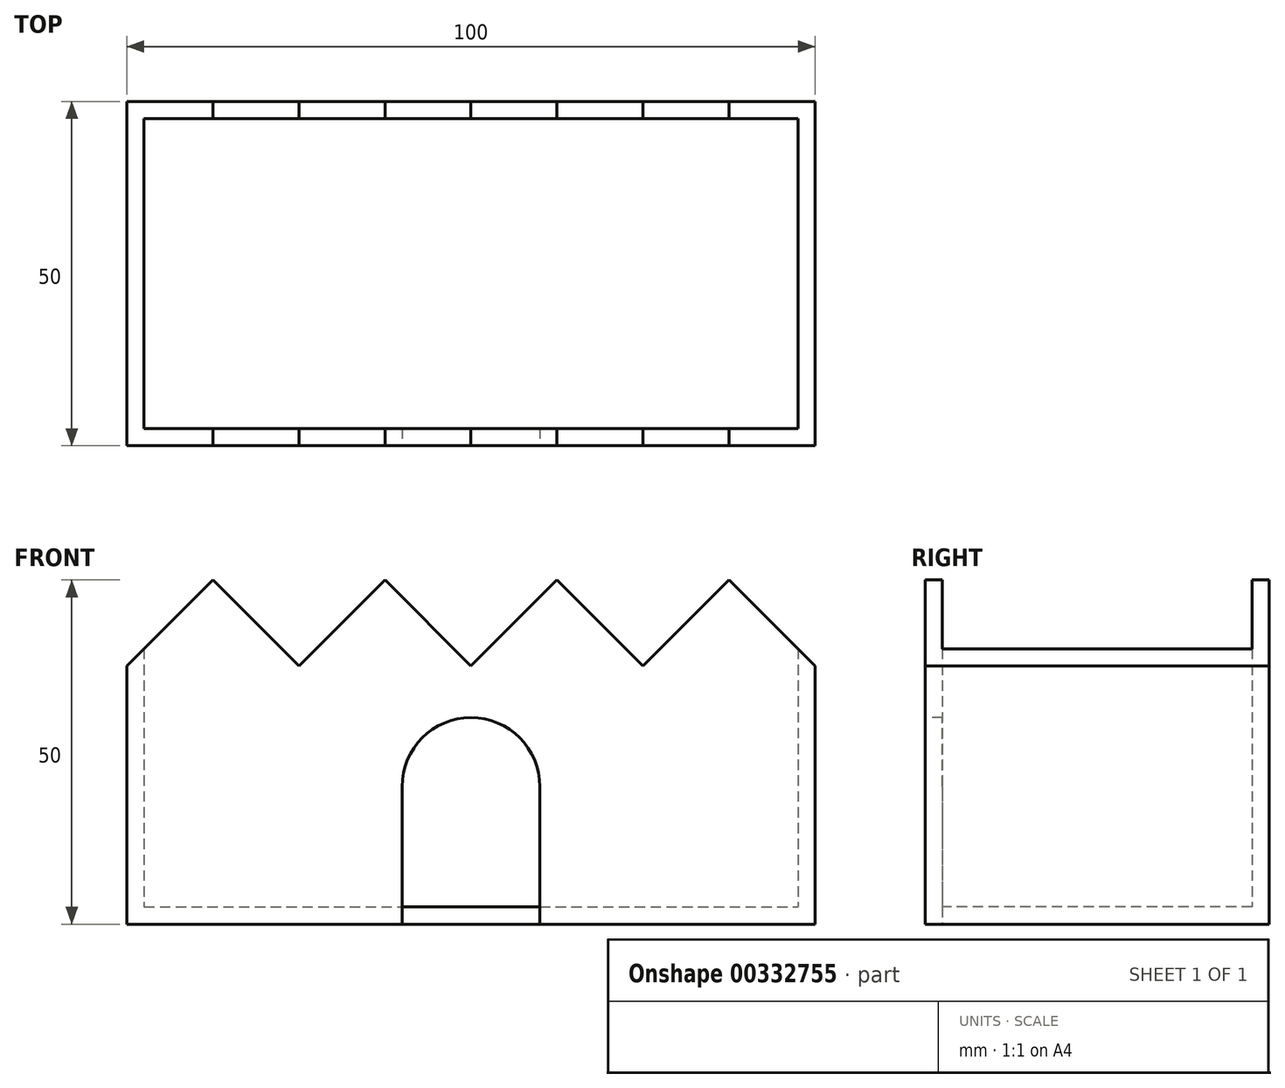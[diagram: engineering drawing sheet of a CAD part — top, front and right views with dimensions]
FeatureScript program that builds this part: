
annotation { "Feature Type Name" : "Feature", "Feature Type Description" : "" }
export const myFeature = defineFeature(function(context is Context, id is Id, definition is map)
    precondition{}
    {
        {
            var Q0;
            Q0=qCreatedBy(makeId("Top.planeOp"),FACE);
            var sketch = newSketch(context, id + "F0", { "sketchPlane" : qUnion([Q0])});
            skLineSegment(sketch, "E0.bottom", {"start": v(-50, 25) * mm, "end": v(50, 25) * mm});
            skLineSegment(sketch, "E0.top", {"start": v(-50, -25) * mm, "end": v(50, -25) * mm});
            skLineSegment(sketch, "E0.left", {"start": v(-50, 25) * mm, "end": v(-50, -25) * mm});
            skLineSegment(sketch, "E0.right", {"start": v(50, 25) * mm, "end": v(50, -25) * mm});
            skPoint(sketch, "E0.middle", {"position": v(0, 0) * mm});
            skSolve(sketch);
        }
        {
            var Q0;
            Q0=makeQuery(id+"F0.imprint","IMPRINT",FACE,{"disambiguationData":[TD([[makeQuery(id+"F0.imprint","IMPRINT",EDGE,{"derivedFrom":sQuery(id+"F0.wireOp",EDGE,"E0.bottom")}),-1.0]])]});
            extrude(context, id + "F1", {"entities" : qUnion([Q0]), "depth" : 50 * mm});
        }
        {
            var Q0;
            Q0=makeQuery(id+"F1.opExtrude","SWEPT_FACE",FACE,{"disambiguationData":[OSD([sQuery(id+"F0.wireOp",EDGE,"E0.top")])]});
            var sketch = newSketch(context, id + "F2", { "sketchPlane" : qUnion([Q0])});
            skLineSegment(sketch, "E1", {"start": v(-50, 37.5) * mm, "end": v(-37.5, 50) * mm});
            skLineSegment(sketch, "E2", {"start": v(-37.5, 50) * mm, "end": v(-25, 37.5) * mm});
            skLineSegment(sketch, "E3", {"start": v(-25, 37.5) * mm, "end": v(-12.5, 50) * mm});
            skLineSegment(sketch, "E4", {"start": v(-12.5, 50) * mm, "end": v(0, 37.5) * mm});
            skLineSegment(sketch, "E5", {"start": v(0, 37.5) * mm, "end": v(12.5, 50) * mm});
            skLineSegment(sketch, "E6", {"start": v(12.5, 50) * mm, "end": v(25, 37.5) * mm});
            skLineSegment(sketch, "E7", {"start": v(25, 37.5) * mm, "end": v(37.5, 50) * mm});
            skLineSegment(sketch, "E8", {"start": v(37.5, 50) * mm, "end": v(50, 37.5) * mm});
            skSolve(sketch);
        }
        {
            var Q0;
            Q0 = qSketchRegion(id + "F2", true);
            var Q1;
            {var subQ0=sQuery(id+"F2.wireOp",EDGE,"E1");Q1=makeQuery(id+"F2.imprint","IMPRINT",FACE,{"disambiguationData":[TD([[makeQuery(id+"F2.imprint","IMPRINT",EDGE,{"derivedFrom":subQ0}),1.0]])]});}
            var Q2;
            {var subQ0=sQuery(id+"F2.wireOp",EDGE,"E2");Q2=makeQuery(id+"F2.imprint","IMPRINT",FACE,{"disambiguationData":[TD([[makeQuery(id+"F2.imprint","IMPRINT",EDGE,{"derivedFrom":subQ0}),1.0]])]});}
            var Q3;
            {var subQ0=sQuery(id+"F2.wireOp",EDGE,"E4");Q3=makeQuery(id+"F2.imprint","IMPRINT",FACE,{"disambiguationData":[TD([[makeQuery(id+"F2.imprint","IMPRINT",EDGE,{"derivedFrom":subQ0}),1.0]])]});}
            var Q4;
            {var subQ0=sQuery(id+"F2.wireOp",EDGE,"E6");Q4=makeQuery(id+"F2.imprint","IMPRINT",FACE,{"disambiguationData":[TD([[makeQuery(id+"F2.imprint","IMPRINT",EDGE,{"derivedFrom":subQ0}),1.0]])]});}
            var Q5;
            {var subQ0=sQuery(id+"F2.wireOp",EDGE,"E8");Q5=makeQuery(id+"F2.imprint","IMPRINT",FACE,{"disambiguationData":[TD([[makeQuery(id+"F2.imprint","IMPRINT",EDGE,{"derivedFrom":subQ0}),1.0]])]});}
            var Q6;
            Q6=makeQuery(id+"F1.opExtrude","SWEPT_BODY",BODY,{"disambiguationData":[OSD([sQuery(id+"F0.wireOp",EDGE,"E0.bottom"),sQuery(id+"F0.wireOp",EDGE,"E0.top"),sQuery(id+"F0.wireOp",EDGE,"E0.left"),sQuery(id+"F0.wireOp",EDGE,"E0.right")])]});
            extrude(context, id + "F3", {"entities" : qUnion([Q0, Q1, Q2, Q3, Q4, Q5]), "operationType" : NewBodyOperationType.REMOVE, "endBound" : BoundingType.UP_TO_BODY, "oppositeDirection" : true, "endBoundEntityBody" : qUnion([Q6]), "depth" : 25 * mm});
        }
        {
            var Q0;
            Q0=makeQuery(id+"F3.boolean.opBoolean","COPY",FACE,{"derivedFrom":makeQuery(id+"F3.opExtrude","SWEPT_FACE",FACE,{"disambiguationData":[OSD([sQuery(id+"F2.wireOp",EDGE,"E2")])]})});
            var Q1;
            Q1=makeQuery(id+"F3.boolean.opBoolean","COPY",FACE,{"derivedFrom":makeQuery(id+"F3.opExtrude","SWEPT_FACE",FACE,{"disambiguationData":[OSD([sQuery(id+"F2.wireOp",EDGE,"E4")])]})});
            var Q2;
            Q2=makeQuery(id+"F3.boolean.opBoolean","COPY",FACE,{"derivedFrom":makeQuery(id+"F3.opExtrude","SWEPT_FACE",FACE,{"disambiguationData":[OSD([sQuery(id+"F2.wireOp",EDGE,"E6")])]})});
            var Q3;
            Q3=makeQuery(id+"F3.boolean.opBoolean","COPY",FACE,{"derivedFrom":makeQuery(id+"F3.opExtrude","SWEPT_FACE",FACE,{"disambiguationData":[OSD([sQuery(id+"F2.wireOp",EDGE,"E8")])]})});
            var Q4;
            Q4=makeQuery(id+"F3.boolean.opBoolean","COPY",FACE,{"derivedFrom":makeQuery(id+"F3.opExtrude","SWEPT_FACE",FACE,{"disambiguationData":[OSD([sQuery(id+"F2.wireOp",EDGE,"E7")])]})});
            var Q5;
            Q5=makeQuery(id+"F3.boolean.opBoolean","COPY",FACE,{"derivedFrom":makeQuery(id+"F3.opExtrude","SWEPT_FACE",FACE,{"disambiguationData":[OSD([sQuery(id+"F2.wireOp",EDGE,"E5")])]})});
            var Q6;
            Q6=makeQuery(id+"F3.boolean.opBoolean","COPY",FACE,{"derivedFrom":makeQuery(id+"F3.opExtrude","SWEPT_FACE",FACE,{"disambiguationData":[OSD([sQuery(id+"F2.wireOp",EDGE,"E3")])]})});
            var Q7;
            Q7=makeQuery(id+"F3.boolean.opBoolean","COPY",FACE,{"derivedFrom":makeQuery(id+"F3.opExtrude","SWEPT_FACE",FACE,{"disambiguationData":[OSD([sQuery(id+"F2.wireOp",EDGE,"E1")])]})});
            shell(context, id + "F4", {"entities" : qUnion([Q0, Q1, Q2, Q3, Q4, Q5, Q6, Q7]), "thickness" : 2.5 * mm});
        }
        {
            var Q0;
            Q0=makeQuery(id+"F1.opExtrude","SWEPT_FACE",FACE,{"disambiguationData":[OSD([sQuery(id+"F0.wireOp",EDGE,"E0.top")])]});
            var sketch = newSketch(context, id + "F5", { "sketchPlane" : qUnion([Q0])});
            skCircle(sketch, "E9", {"center": v(0, 20) * mm, "radius": 10 * mm});
            skLineSegment(sketch, "E10.bottom", {"start": v(-10, 20) * mm, "end": v(10, 20) * mm});
            skLineSegment(sketch, "E10.top", {"start": v(-10, 0) * mm, "end": v(10, 0) * mm});
            skLineSegment(sketch, "E10.left", {"start": v(-10, 20) * mm, "end": v(-10, 0) * mm});
            skLineSegment(sketch, "E10.right", {"start": v(10, 20) * mm, "end": v(10, 0) * mm});
            skPoint(sketch, "E10.middle", {"position": v(0, 10) * mm});
            skLineSegment(sketch, "E11.bottom", {"start": v(-10, 2.5) * mm, "end": v(10, 2.5) * mm});
            skLineSegment(sketch, "E11.left", {"start": v(-10, 2.5) * mm, "end": v(-10, 0) * mm});
            skLineSegment(sketch, "E11.right", {"start": v(10, 2.5) * mm, "end": v(10, 0) * mm});
            skPoint(sketch, "E11.middle", {"position": v(0, 1.25) * mm});
            skSolve(sketch);
        }
        {
            var Q0;
            {var subQ0=sQuery(id+"F5.wireOp",EDGE,"E10.bottom");Q0=makeQuery(id+"F5.imprint","IMPRINT",FACE,{"disambiguationData":[TD([[makeQuery(id+"F5.imprint","IMPRINT",EDGE,{"derivedFrom":subQ0}),-1.0]])]});}
            var Q1;
            {var subQ0=sQuery(id+"F5.wireOp",EDGE,"E10.bottom");Q1=makeQuery(id+"F5.imprint","IMPRINT",FACE,{"disambiguationData":[TD([[makeQuery(id+"F5.imprint","IMPRINT",EDGE,{"derivedFrom":subQ0}),1.0]])]});}
            var Q2;
            {var subQ0=sQuery(id+"F5.wireOp",EDGE,"E10.left");Q2=makeQuery(id+"F5.imprint","IMPRINT",FACE,{"disambiguationData":[TD([[makeQuery(id+"F5.imprint","IMPRINT",EDGE,{"derivedFrom":subQ0}),1.0]])]});}
            var Q3;
            Q3=makeQuery(id+"F4.opShell","OFFSET_FACE",FACE,{"disambiguationData":[OSD([sQuery(id+"F0.wireOp",EDGE,"E0.top")])]});
            extrude(context, id + "F6", {"entities" : qUnion([Q0, Q1, Q2]), "operationType" : NewBodyOperationType.REMOVE, "endBound" : BoundingType.UP_TO_SURFACE, "oppositeDirection" : true, "endBoundEntityFace" : qUnion([Q3]), "depth" : 25 * mm});
        }
    });
